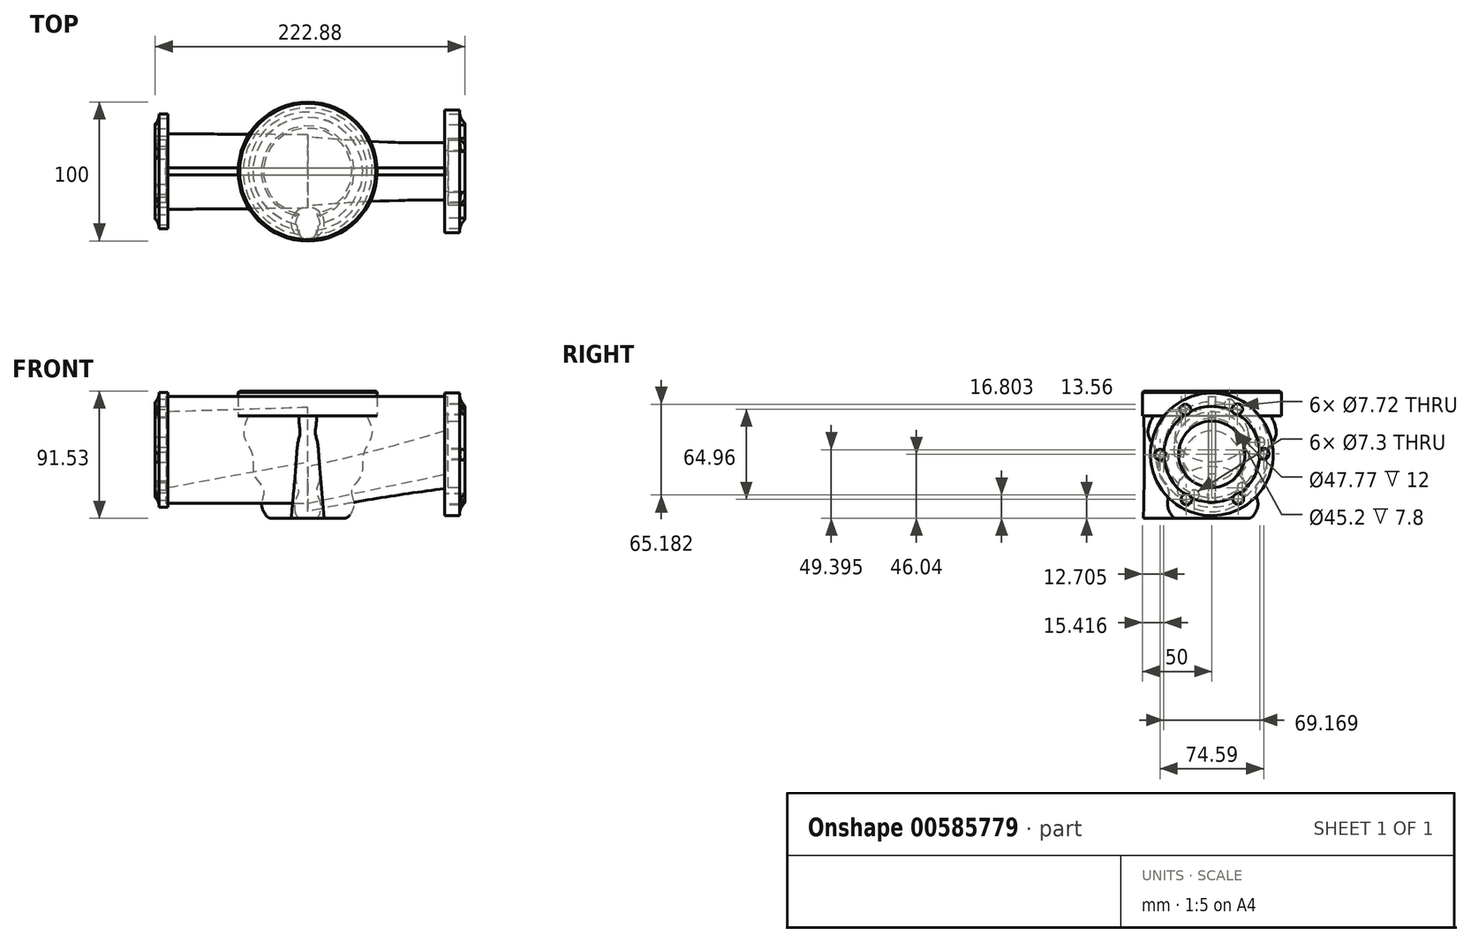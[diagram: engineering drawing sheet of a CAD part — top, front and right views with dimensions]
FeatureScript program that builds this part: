
annotation { "Feature Type Name" : "Feature", "Feature Type Description" : "" }
export const myFeature = defineFeature(function(context is Context, id is Id, definition is map)
    precondition{}
    {
        {
            var Q0;
            Q0=qCreatedBy(makeId("Top.planeOp"),FACE);
            var sketch = newSketch(context, id + "F0", { "sketchPlane" : qUnion([Q0])});
            skCircle(sketch, "E0", {"center": v(0, 0) * mm, "radius": 50 * mm});
            skSolve(sketch);
        }
        {
            var Q0;
            Q0 = qSketchRegion(id + "F0", true);
            extrude(context, id + "F1", {"entities" : qUnion([Q0]), "depth" : 18 * mm, "offsetDistance" : 25 * mm});
        }
        {
            var Q0;
            Q0=qCreatedBy(makeId("Front.planeOp"),FACE);
            var sketch = newSketch(context, id + "F2", { "sketchPlane" : qUnion([Q0])});
            skFitSpline(sketch, "E1", {"points": [v(-42.73, 0) * mm, v(-45.64, -15.33) * mm, v(-39.65, -28.58) * mm, v(-38.56, -42.37) * mm, v(-31.67, -53.24) * mm, v(-33.18, -63.17) * mm, v(-28.65, -73.53) * mm], "startDerivative": vector(-57.46, -125.5) * mm, "endDerivative": vector(45.6, -65.45) * mm});
            skLineSegment(sketch, "E2", {"start": v(-28.65, -73.53) * mm, "end": v(0, -73.53) * mm});
            skLineSegment(sketch, "E3", {"start": v(0, -73.53) * mm, "end": v(0, 0) * mm});
            skLineSegment(sketch, "E4", {"start": v(0, 0) * mm, "end": v(-42.73, 0) * mm});
            skSolve(sketch);
        }
        {
            var Q0;
            Q0 = qSketchRegion(id + "F2", true);
            var Q1;
            Q1=sQuery(id+"F2.wireOp",EDGE,"E3");
            revolve(context, id + "F3", {"operationType" : NewBodyOperationType.ADD, "entities" : qUnion([Q0]), "axis" : qUnion([Q1]), "revolveType" : RevolveType.FULL});
        }
        {
            var Q0;
            Q0=qCreatedBy(makeId("Right.planeOp"),FACE);
            var sketch = newSketch(context, id + "F4", { "sketchPlane" : qUnion([Q0])});
            skEllipse(sketch, "E5", {"center": v(0, -52.55) * mm, "majorRadius": 24.86 * mm, "minorRadius": 16.14 * mm, "majorAxis": v(1, 0)});
            skSolve(sketch);
        }
        {
            var Q0;
            Q0=qCreatedBy(makeId("Front.planeOp"),FACE);
            var sketch = newSketch(context, id + "F5", { "sketchPlane" : qUnion([Q0])});
            skLineSegment(sketch, "E6.bottom", {"start": v(98.62, -71.58) * mm, "end": v(109.14, -71.58) * mm});
            skLineSegment(sketch, "E6.top", {"start": v(98.62, -27.49) * mm, "end": v(113.14, -27.49) * mm});
            skLineSegment(sketch, "E6.left", {"start": v(98.62, -71.58) * mm, "end": v(98.62, -27.49) * mm});
            skFitSpline(sketch, "E7", {"points": [v(109.14, -71.58) * mm, v(113.14, -61.97) * mm], "startDerivative": vector(0, 14.15) * mm, "endDerivative": vector(6.53, 8.17) * mm});
            skLineSegment(sketch, "E8", {"start": v(113.14, -61.97) * mm, "end": v(113.14, -27.49) * mm});
            skSolve(sketch);
        }
        {
            var Q0;
            Q0 = qSketchRegion(id + "F5", true);
            var Q1;
            Q1=sQuery(id+"F5.wireOp",EDGE,"E6.top");
            revolve(context, id + "F6", {"entities" : qUnion([Q0]), "axis" : qUnion([Q1]), "revolveType" : RevolveType.FULL});
        }
        {
            var Q0;
            Q0=makeQuery(id+"F6.opRevolve","SWEPT_FACE",FACE,{"disambiguationData":[OSD([sQuery(id+"F5.wireOp",EDGE,"E6.left")])]});
            var sketch = newSketch(context, id + "F7", { "sketchPlane" : qUnion([Q0])});
            skCircle(sketch, "E9", {"center": v(0, -31.4) * mm, "radius": 20.7 * mm});
            skSolve(sketch);
        }
        {
            var Q0;
            Q0 = qSketchRegion(id + "F4", true);
            var Q1;
            Q1 = qSketchRegion(id + "F7", true);
            var Q2;
            Q2 = qConstructionFilter(qBodyType(qCreatedBy(id + "FC9hj8aCEs09jKz_2" ,EDGE), BodyType.WIRE), ConstructionObject.NO);
            var Q3;
            Q3=sQuery(id+"F4.wireOp",VERTEX,"E5.center");
            var Q4;
            Q4=sQuery(id+"F7.wireOp",VERTEX,"E9.center");
            loft(context, id + "F8", {"sheetProfilesArray" : [{ "sheetProfileEntities" : qUnion([Q0]) }, { "sheetProfileEntities" : qUnion([Q1]) }], "guidesArray" : [{ "guideEntities" : qUnion([Q2]), "guideDerivativeType" : LoftGuideDerivativeType.DEFAULT, "guideDerivativeMagnitude" : 1 }], "connections" : [{ "connectionEntities" : qUnion([Q3, Q4]), "connectionEdgeQueries" : qUnion([]), "connectionEdgeParameters" : [] }]});
        }
        {
            var Q0;
            Q0=qCreatedBy(makeId("Front.planeOp"),FACE);
            var sketch = newSketch(context, id + "F9", { "sketchPlane" : qUnion([Q0])});
            skLineSegment(sketch, "E10.bottom", {"start": v(-100.67, -24.14) * mm, "end": v(-109.74, -24.14) * mm});
            skLineSegment(sketch, "E10.top", {"start": v(-100.67, -65.41) * mm, "end": v(-106.84, -65.41) * mm});
            skLineSegment(sketch, "E10.left", {"start": v(-100.67, -24.14) * mm, "end": v(-100.67, -65.41) * mm});
            skLineSegment(sketch, "E11", {"start": v(-109.74, -24.14) * mm, "end": v(-109.74, -58.52) * mm});
            skFitSpline(sketch, "E12", {"points": [v(-109.74, -58.52) * mm, v(-106.84, -65.41) * mm], "startDerivative": vector(6.07, -4.35) * mm, "endDerivative": vector(0.46, -7.08) * mm});
            skSolve(sketch);
        }
        {
            var Q0;
            Q0 = qSketchRegion(id + "F9", true);
            var Q1;
            Q1=sQuery(id+"F9.wireOp",EDGE,"E10.bottom");
            revolve(context, id + "F10", {"entities" : qUnion([Q0]), "axis" : qUnion([Q1]), "revolveType" : RevolveType.FULL});
        }
        {
            var Q0;
            Q0=qCreatedBy(makeId("Right.planeOp"),FACE);
            var sketch = newSketch(context, id + "F11", { "sketchPlane" : qUnion([Q0])});
            skEllipse(sketch, "E13", {"center": v(0, -13.34) * mm, "majorRadius": 26.4 * mm, "minorRadius": 19.55 * mm, "majorAxis": v(-1, 0)});
            skSolve(sketch);
        }
        {
            var Q0;
            Q0=makeQuery(id+"F10.opRevolve","SWEPT_FACE",FACE,{"disambiguationData":[OSD([sQuery(id+"F9.wireOp",EDGE,"E10.left")])]});
            var sketch = newSketch(context, id + "F12", { "sketchPlane" : qUnion([Q0])});
            skCircle(sketch, "E14", {"center": v(0, -24.14) * mm, "radius": 27.2 * mm});
            skSolve(sketch);
        }
        {
            var Q0;
            Q0 = qSketchRegion(id + "F12", true);
            var Q1;
            Q1 = qSketchRegion(id + "F11", true);
            loft(context, id + "F13", {"sheetProfilesArray" : [{ "sheetProfileEntities" : qUnion([Q0]) }, { "sheetProfileEntities" : qUnion([Q1]) }]});
        }
        {
            var Q0;
            Q0=qCreatedBy(makeId("Front.planeOp"),FACE);
            var sketch = newSketch(context, id + "F14", { "sketchPlane" : qUnion([Q0])});
            skLineSegment(sketch, "E15", {"start": v(-102.18, 14.24) * mm, "end": v(100.5, 14.24) * mm});
            skLineSegment(sketch, "E16", {"start": v(100.5, 14.24) * mm, "end": v(100.5, -41.46) * mm});
            skLineSegment(sketch, "E17", {"start": v(-102.18, 14.24) * mm, "end": v(-102.18, -62.7) * mm});
            skLineSegment(sketch, "E18", {"start": v(-102.18, -62.7) * mm, "end": v(0, -62.7) * mm});
            skLineSegment(sketch, "E19", {"start": v(0, -62.7) * mm, "end": v(100.5, -41.46) * mm});
            skSolve(sketch);
        }
        {
            var Q0;
            Q0 = qSketchRegion(id + "F14", true);
            extrude(context, id + "F15", {"entities" : qUnion([Q0]), "endBound" : BoundingType.SYMMETRIC, "depth" : 5 * mm, "offsetDistance" : 25 * mm});
        }
        {
            var Q0;
            Q0=makeQuery(id+"F1.opExtrude","CAP_FACE",FACE,{"disambiguationData":[OSD([sQuery(id+"F0.wireOp",EDGE,"E0")])],"isStart":true});
            var sketch = newSketch(context, id + "F16", { "sketchPlane" : qUnion([Q0])});
            skCircle(sketch, "E20", {"center": v(0, 42.73) * mm, "radius": 6.33 * mm});
            skSolve(sketch);
        }
        {
            var Q0;
            Q0=makeQuery(id+"F3.opRevolve","SWEPT_FACE",FACE,{"disambiguationData":[OSD([sQuery(id+"F2.wireOp",EDGE,"E2")])]});
            var sketch = newSketch(context, id + "F17", { "sketchPlane" : qUnion([Q0])});
            skCircle(sketch, "E21", {"center": v(0, 37.29) * mm, "radius": 11.9 * mm});
            skSolve(sketch);
        }
        {
            var Q1;
            Q1 = qSketchRegion(id + "F16", true);
            var Q2;
            Q2 = qSketchRegion(id + "F17", true);
            loft(context, id + "F18", {"operationType" : NewBodyOperationType.ADD, "sheetProfilesArray" : [{ "sheetProfileEntities" : qUnion([Q1]) }, { "sheetProfileEntities" : qUnion([Q2]) }]});
        }
        {
            var Q0;
            Q0=makeQuery(id+"F6.opRevolve","SWEPT_FACE",FACE,{"disambiguationData":[OSD([sQuery(id+"F5.wireOp",EDGE,"E6.left")])]});
            var sketch = newSketch(context, id + "F19", { "sketchPlane" : qUnion([Q0])});
            skCircle(sketch, "E22", {"center": v(18.96, 4.63) * mm, "radius": 3.86 * mm});
            skCircle(sketch, "E23.1.0", {"center": v(37.3, -27.85) * mm, "radius": 3.86 * mm});
            skCircle(sketch, "E23.2.0", {"center": v(18.33, -59.97) * mm, "radius": 3.86 * mm});
            skCircle(sketch, "E23.3.0", {"center": v(-18.96, -59.6) * mm, "radius": 3.86 * mm});
            skCircle(sketch, "E23.4.0", {"center": v(-37.3, -27.13) * mm, "radius": 3.86 * mm});
            skCircle(sketch, "E23.5.0", {"center": v(-18.33, 4.99) * mm, "radius": 3.86 * mm});
            skPoint(sketch, "E23.center", {"position": v(0, -27.49) * mm});
            skLineSegment(sketch, "E23.anchor1", {"start": v(0, -27.49) * mm, "end": v(18.96, 4.63) * mm, "construction": true});
            skLineSegment(sketch, "E23.anchor2", {"start": v(0, -27.49) * mm, "end": v(-18.33, 4.99) * mm, "construction": true});
            skSolve(sketch);
        }
        {
            var Q0;
            Q0 = qSketchRegion(id + "F19", true);
            extrude(context, id + "F20", {"entities" : qUnion([Q0]), "operationType" : NewBodyOperationType.REMOVE, "oppositeDirection" : true, "depth" : 25 * mm, "offsetDistance" : 25 * mm});
        }
        {
            var Q0;
            Q0=makeQuery(id+"F10.opRevolve","SWEPT_FACE",FACE,{"disambiguationData":[OSD([sQuery(id+"F9.wireOp",EDGE,"E10.left")])]});
            var sketch = newSketch(context, id + "F21", { "sketchPlane" : qUnion([Q0])});
            skCircle(sketch, "E24", {"center": v(-21.86, 3.18) * mm, "radius": 3.65 * mm});
            skCircle(sketch, "E25.1.0", {"center": v(-34.58, -29.42) * mm, "radius": 3.65 * mm});
            skCircle(sketch, "E25.2.0", {"center": v(-12.72, -56.73) * mm, "radius": 3.65 * mm});
            skCircle(sketch, "E25.3.0", {"center": v(21.86, -51.45) * mm, "radius": 3.65 * mm});
            skCircle(sketch, "E25.4.0", {"center": v(34.58, -18.86) * mm, "radius": 3.65 * mm});
            skCircle(sketch, "E25.5.0", {"center": v(12.72, 8.46) * mm, "radius": 3.65 * mm});
            skPoint(sketch, "E25.center", {"position": v(0, -24.14) * mm});
            skSolve(sketch);
        }
        {
            var Q0;
            Q0 = qSketchRegion(id + "F21", true);
            extrude(context, id + "F22", {"entities" : qUnion([Q0]), "operationType" : NewBodyOperationType.REMOVE, "oppositeDirection" : true, "depth" : 25 * mm, "offsetDistance" : 25 * mm});
        }
        {
            var Q0;
            Q0=makeQuery(id+"F6.opRevolve","SWEPT_FACE",FACE,{"disambiguationData":[OSD([sQuery(id+"F5.wireOp",EDGE,"E8")])]});
            var sketch = newSketch(context, id + "F23", { "sketchPlane" : qUnion([Q0])});
            skCircle(sketch, "E26", {"center": v(0, -27.49) * mm, "radius": 23.88 * mm});
            skSolve(sketch);
        }
        {
            var Q0;
            Q0 = qSketchRegion(id + "F23", true);
            extrude(context, id + "F24", {"entities" : qUnion([Q0]), "operationType" : NewBodyOperationType.REMOVE, "oppositeDirection" : true, "depth" : 12 * mm, "offsetDistance" : 25 * mm});
        }
        {
            var Q0;
            Q0=makeQuery(id+"F10.opRevolve","SWEPT_FACE",FACE,{"disambiguationData":[OSD([sQuery(id+"F9.wireOp",EDGE,"E11")])]});
            var sketch = newSketch(context, id + "F25", { "sketchPlane" : qUnion([Q0])});
            skCircle(sketch, "E27", {"center": v(0, -24.14) * mm, "radius": 22.6 * mm});
            skSolve(sketch);
        }
        {
            var Q0;
            Q0 = qSketchRegion(id + "F25", true);
            extrude(context, id + "F26", {"entities" : qUnion([Q0]), "operationType" : NewBodyOperationType.REMOVE, "oppositeDirection" : true, "depth" : 7.8 * mm, "offsetDistance" : 25 * mm});
        }
        {
            var Q0;
            Q0=makeQuery(id+"F1.opExtrude","CAP_EDGE",EDGE,{"disambiguationData":[OSD([sQuery(id+"F0.wireOp",EDGE,"E0")])],"isStart":false});
            chamfer(context, id + "F27", {"entities" : qUnion([Q0]), "width" : 1 * mm, "tangentPropagation" : true});
        }
        {
            var Q0;
            Q0=makeQuery(id+"F3.opRevolve","SWEPT_EDGE",EDGE,{"disambiguationData":[OSD([sQuery(id+"F2.wireOp",EDGE,"E1"),sQuery(id+"F2.wireOp",EDGE,"E2")])]});
            fillet(context, id + "F28", {"entities" : qUnion([Q0]), "radius" : 5 * mm, "tangentPropagation" : true, "allowEdgeOverflow" : false});
        }
    });
